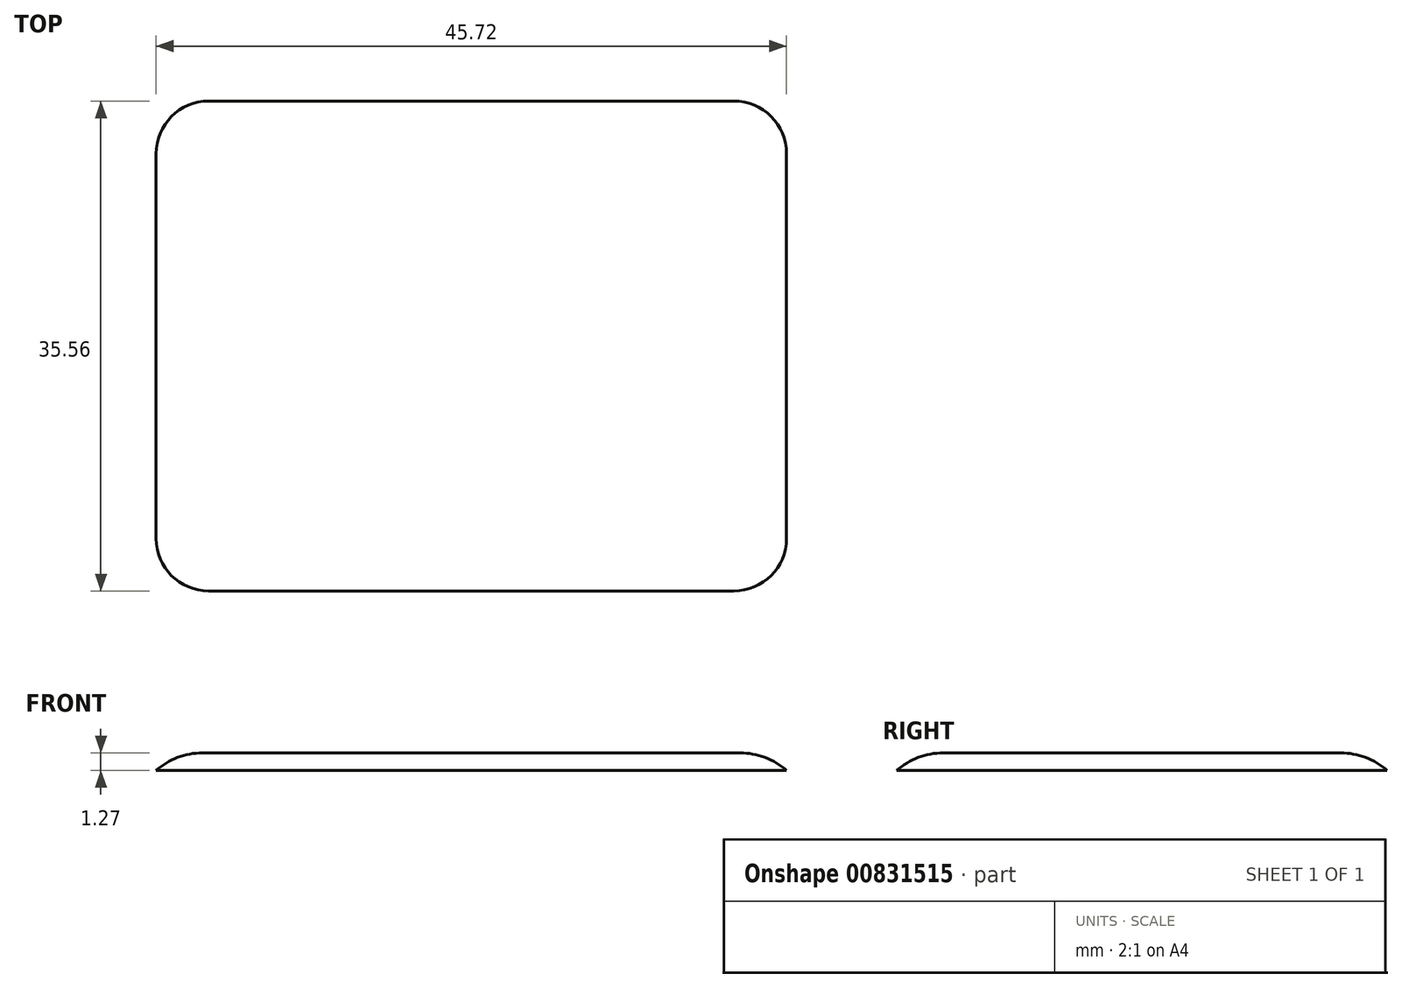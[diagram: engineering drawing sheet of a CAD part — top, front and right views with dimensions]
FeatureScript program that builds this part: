
annotation { "Feature Type Name" : "Feature", "Feature Type Description" : "" }
export const myFeature = defineFeature(function(context is Context, id is Id, definition is map)
    precondition{}
    {
        {
            var Q0;
            Q0=qCreatedBy(makeId("Top.planeOp"),FACE);
            var sketch = newSketch(context, id + "F0", { "sketchPlane" : qUnion([Q0])});
            skLineSegment(sketch, "E0.bottom", {"start": v(19.05, 17.78) * mm, "end": v(-19.05, 17.78) * mm});
            skLineSegment(sketch, "E0.top", {"start": v(19.05, -17.78) * mm, "end": v(-19.05, -17.78) * mm});
            skLineSegment(sketch, "E0.left", {"start": v(22.86, 13.97) * mm, "end": v(22.86, -13.97) * mm});
            skLineSegment(sketch, "E0.right", {"start": v(-22.86, 13.97) * mm, "end": v(-22.86, -13.97) * mm});
            skPoint(sketch, "E0.middle", {"position": v(0, 0) * mm});
            skPoint(sketch, "E1.visualSharp", {"position": v(-22.86, 17.78) * mm});
            skArc(sketch, "E1.filletArc", {"start": v(-19.05, 17.78) * mm, "mid": v(-21.74, 16.66) * mm, "end": v(-22.86, 13.97) * mm});
            skPoint(sketch, "E2.visualSharp", {"position": v(22.86, 17.78) * mm});
            skArc(sketch, "E2.filletArc", {"start": v(22.86, 13.97) * mm, "mid": v(21.74, 16.66) * mm, "end": v(19.05, 17.78) * mm});
            skPoint(sketch, "E3.visualSharp", {"position": v(22.86, -17.78) * mm});
            skArc(sketch, "E3.filletArc", {"start": v(19.05, -17.78) * mm, "mid": v(21.74, -16.66) * mm, "end": v(22.86, -13.97) * mm});
            skPoint(sketch, "E4.visualSharp", {"position": v(-22.86, -17.78) * mm});
            skArc(sketch, "E4.filletArc", {"start": v(-22.86, -13.97) * mm, "mid": v(-21.74, -16.66) * mm, "end": v(-19.05, -17.78) * mm});
            skSolve(sketch);
        }
        {
            var Q0;
            Q0 = qSketchRegion(id + "F0", true);
            extrude(context, id + "F1", {"entities" : qUnion([Q0]), "depth" : 1.27 * mm, "offsetDistance" : 25.4 * mm});
        }
        {
            var Q0;
            Q0=makeQuery(id+"F1.opExtrude","CAP_EDGE",EDGE,{"disambiguationData":[OSD([sQuery(id+"F0.wireOp",EDGE,"E0.right")])],"isStart":false});
            fillet(context, id + "F2", {"entities" : qUnion([Q0]), "radius" : 5.08 * mm, "tangentPropagation" : true, "allowEdgeOverflow" : false});
        }
    });
